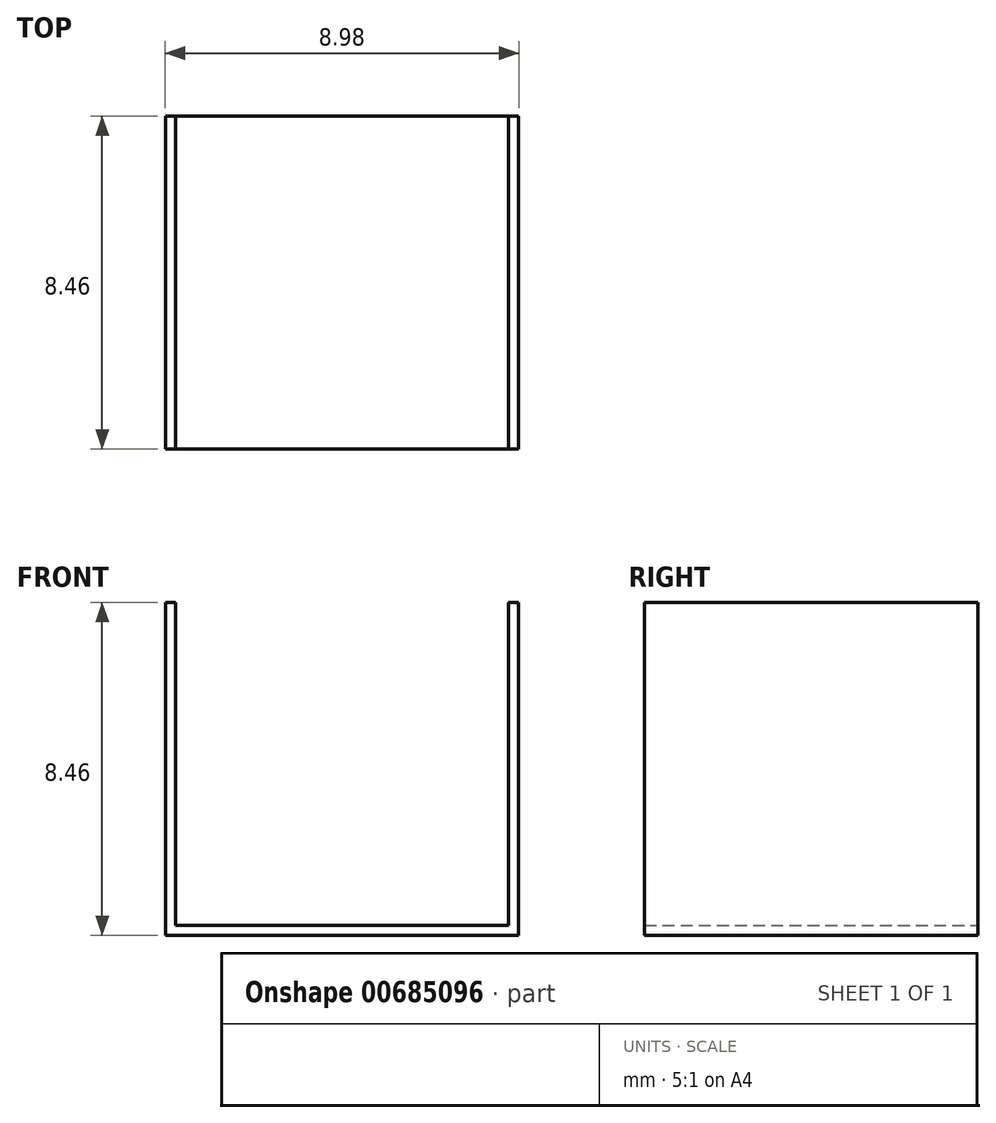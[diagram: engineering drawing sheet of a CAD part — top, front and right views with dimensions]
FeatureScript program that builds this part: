
annotation { "Feature Type Name" : "Feature", "Feature Type Description" : "" }
export const myFeature = defineFeature(function(context is Context, id is Id, definition is map)
    precondition{}
    {
        {
            var Q0;
            Q0=qCreatedBy(makeId("Right.planeOp"),FACE);
            var sketch = newSketch(context, id + "F0", { "sketchPlane" : qUnion([Q0])});
            skLineSegment(sketch, "E0.bottom", {"start": v(-4.23, 4.23) * mm, "end": v(4.23, 4.23) * mm});
            skLineSegment(sketch, "E0.top", {"start": v(-4.23, -4.23) * mm, "end": v(4.23, -4.23) * mm});
            skLineSegment(sketch, "E0.left", {"start": v(-4.23, 4.23) * mm, "end": v(-4.23, -4.23) * mm});
            skLineSegment(sketch, "E0.right", {"start": v(4.23, 4.23) * mm, "end": v(4.23, -4.23) * mm});
            skPoint(sketch, "E0.middle", {"position": v(0, 0) * mm});
            skSolve(sketch);
        }
        {
            var Q0;
            Q0 = qSketchRegion(id + "F0", true);
            extrude(context, id + "F1", {"entities" : qUnion([Q0]), "depth" : 0.25 * mm, "offsetDistance" : 25.4 * mm, "symmetric" : true});
        }
        {
            var Q0;
            Q0=makeQuery(id+"F1.opExtrude","SWEPT_FACE",FACE,{"disambiguationData":[OSD([sQuery(id+"F0.wireOp",EDGE,"E0.top")])]});
            var sketch = newSketch(context, id + "F2", { "sketchPlane" : qUnion([Q0])});
            skLineSegment(sketch, "E1.0", {"start": v(0.13, 4.23) * mm, "end": v(0.13, -4.23) * mm});
            skLineSegment(sketch, "E2", {"start": v(0.13, 4.23) * mm, "end": v(8.6, 4.23) * mm});
            skLineSegment(sketch, "E3", {"start": v(8.6, 4.23) * mm, "end": v(8.6, -4.23) * mm});
            skLineSegment(sketch, "E4", {"start": v(8.6, -4.23) * mm, "end": v(0.13, -4.23) * mm});
            skSolve(sketch);
        }
        {
            var Q0;
            Q0 = qSketchRegion(id + "F2", true);
            extrude(context, id + "F3", {"entities" : qUnion([Q0]), "operationType" : NewBodyOperationType.ADD, "oppositeDirection" : true, "depth" : 0.25 * mm, "offsetDistance" : 25.4 * mm});
        }
        {
            var Q0;
            Q0=makeQuery(id+"F3.opExtrude","SWEPT_FACE",FACE,{"disambiguationData":[OSD([sQuery(id+"F2.wireOp",EDGE,"E3")])]});
            var sketch = newSketch(context, id + "F4", { "sketchPlane" : qUnion([Q0])});
            skLineSegment(sketch, "E5.0.0", {"start": v(-4.23, 4.23) * mm, "end": v(-4.23, -3.98) * mm});
            skLineSegment(sketch, "E5.0.1", {"start": v(-4.23, -3.98) * mm, "end": v(4.23, -3.98) * mm});
            skLineSegment(sketch, "E5.0.2", {"start": v(4.23, -3.98) * mm, "end": v(4.23, 4.23) * mm});
            skLineSegment(sketch, "E5.0.3", {"start": v(4.23, 4.23) * mm, "end": v(-4.23, 4.23) * mm});
            skLineSegment(sketch, "E6.0.0", {"start": v(-4.23, -4.23) * mm, "end": v(4.23, -4.23) * mm});
            skLineSegment(sketch, "E6.0.1", {"start": v(4.23, -4.23) * mm, "end": v(4.23, -3.98) * mm});
            skLineSegment(sketch, "E6.0.2", {"start": v(4.23, -3.98) * mm, "end": v(-4.23, -3.98) * mm});
            skLineSegment(sketch, "E6.0.3", {"start": v(-4.23, -3.98) * mm, "end": v(-4.23, -4.23) * mm});
            skSolve(sketch);
        }
        {
            var Q0;
            Q0 = qSketchRegion(id + "F4", true);
            extrude(context, id + "F5", {"entities" : qUnion([Q0]), "operationType" : NewBodyOperationType.ADD, "depth" : 0.25 * mm, "offsetDistance" : 25.4 * mm});
        }
    });
